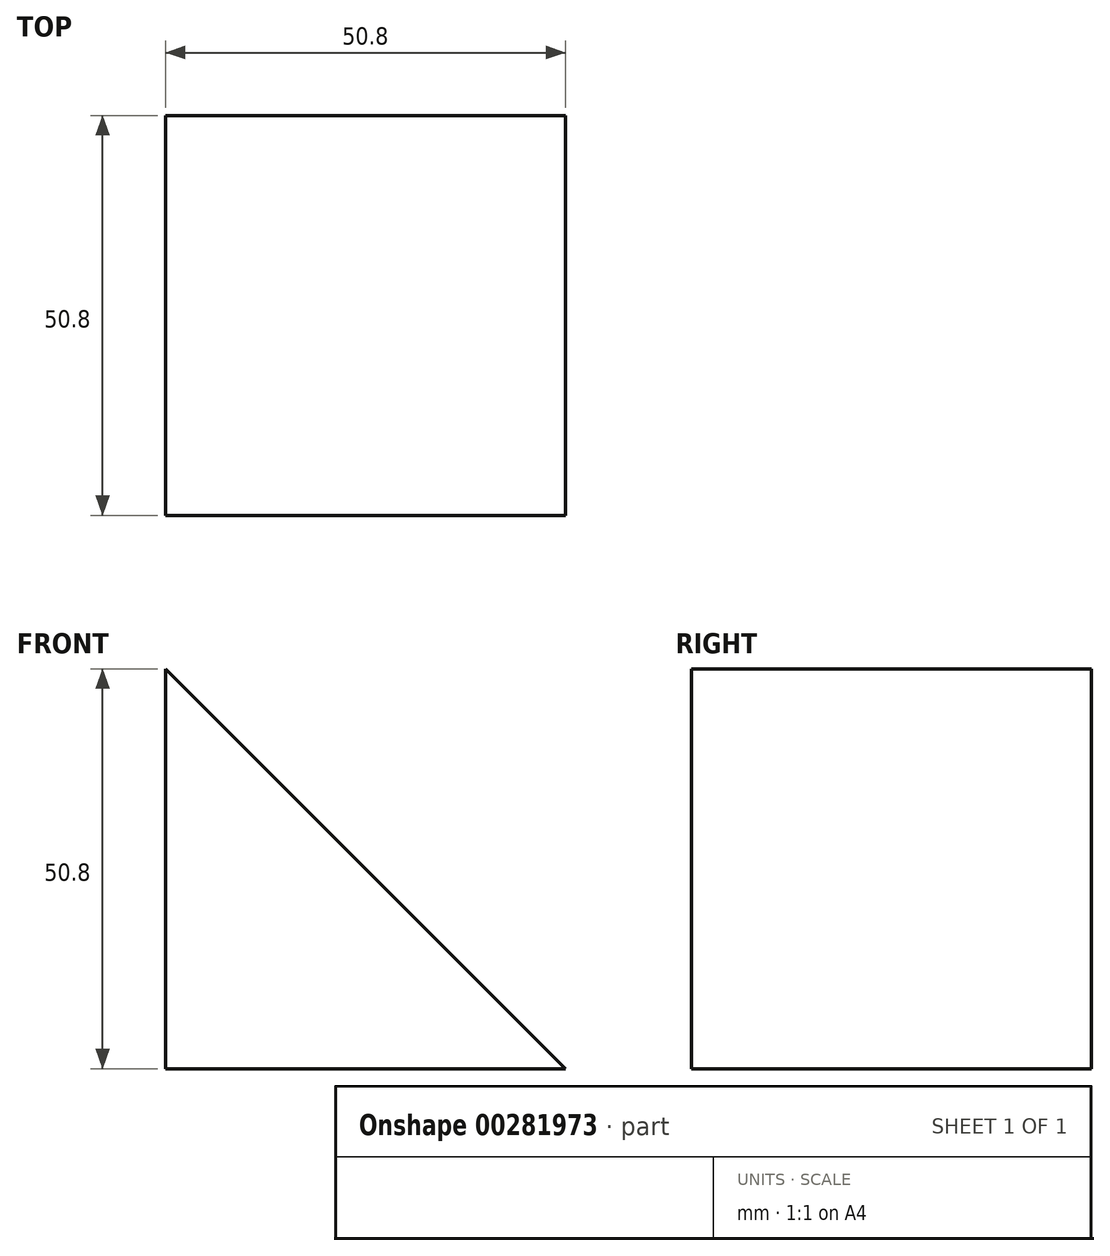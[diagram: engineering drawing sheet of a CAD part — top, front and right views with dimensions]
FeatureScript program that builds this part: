
annotation { "Feature Type Name" : "Feature", "Feature Type Description" : "" }
export const myFeature = defineFeature(function(context is Context, id is Id, definition is map)
    precondition{}
    {
        {
            var Q0;
            Q0=qCreatedBy(makeId("Front.planeOp"),FACE);
            var sketch = newSketch(context, id + "F0", { "sketchPlane" : qUnion([Q0])});
            skLineSegment(sketch, "E0", {"start": v(-57.29, 79.83) * mm, "end": v(-57.29, 29.03) * mm});
            skLineSegment(sketch, "E1", {"start": v(-57.29, 29.03) * mm, "end": v(-6.49, 29.03) * mm});
            skLineSegment(sketch, "E2", {"start": v(-6.49, 29.03) * mm, "end": v(-57.29, 79.83) * mm});
            skSolve(sketch);
        }
        {
            var Q0;
            Q0 = qSketchRegion(id + "F0", true);
            extrude(context, id + "F1", {"entities" : qUnion([Q0]), "depth" : 50.8 * mm});
        }
    });
